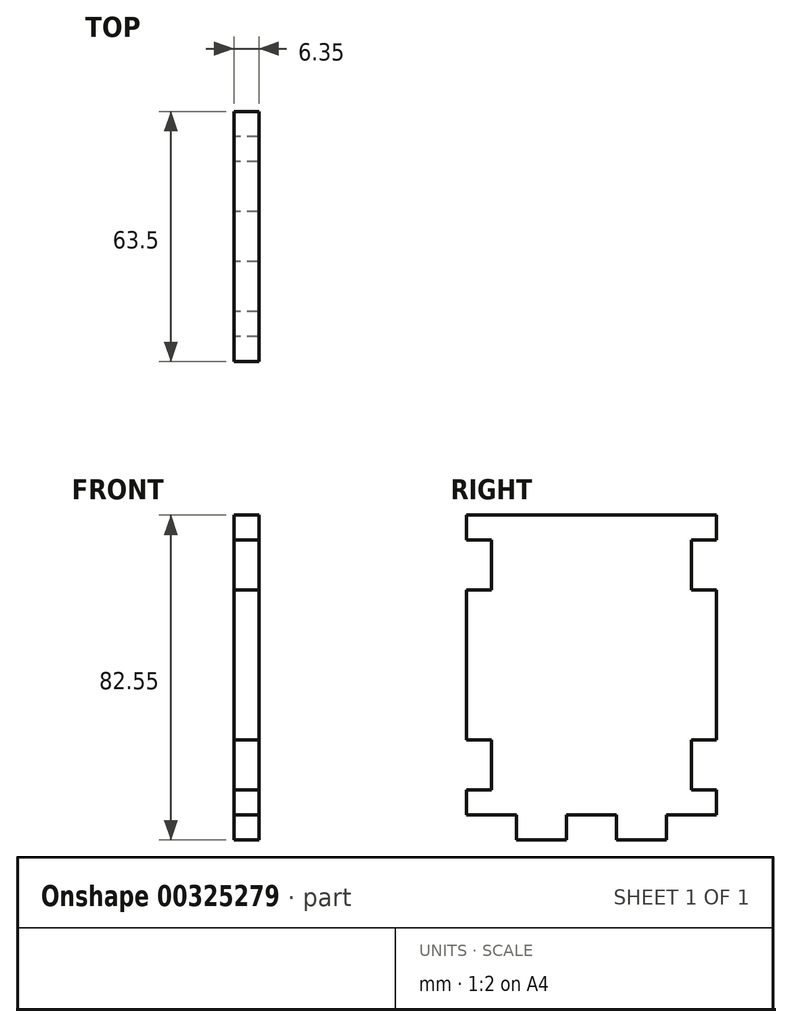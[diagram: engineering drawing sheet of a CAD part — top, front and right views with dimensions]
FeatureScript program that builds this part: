
annotation { "Feature Type Name" : "Feature", "Feature Type Description" : "" }
export const myFeature = defineFeature(function(context is Context, id is Id, definition is map)
    precondition{}
    {
        {
            var Q0;
            Q0=qCreatedBy(makeId("Right.planeOp"),FACE);
            var sketch = newSketch(context, id + "F0", { "sketchPlane" : qUnion([Q0])});
            skLineSegment(sketch, "E0", {"start": v(0, 6.35) * mm, "end": v(12.7, 6.35) * mm});
            skLineSegment(sketch, "E1", {"start": v(12.7, 6.35) * mm, "end": v(12.7, 0) * mm});
            skLineSegment(sketch, "E2", {"start": v(12.7, 0) * mm, "end": v(25.4, 0) * mm});
            skLineSegment(sketch, "E3", {"start": v(25.4, 0) * mm, "end": v(25.4, 6.35) * mm});
            skLineSegment(sketch, "E4", {"start": v(25.4, 6.35) * mm, "end": v(38.1, 6.35) * mm});
            skLineSegment(sketch, "E5", {"start": v(38.1, 6.35) * mm, "end": v(38.1, 0) * mm});
            skLineSegment(sketch, "E6", {"start": v(38.1, 0) * mm, "end": v(50.8, 0) * mm});
            skLineSegment(sketch, "E7", {"start": v(50.8, 0) * mm, "end": v(50.8, 6.35) * mm});
            skLineSegment(sketch, "E8", {"start": v(50.8, 6.35) * mm, "end": v(63.5, 6.35) * mm});
            skLineSegment(sketch, "E9", {"start": v(63.5, 6.35) * mm, "end": v(63.5, 12.7) * mm});
            skLineSegment(sketch, "E10", {"start": v(63.5, 12.7) * mm, "end": v(57.15, 12.7) * mm});
            skLineSegment(sketch, "E11", {"start": v(57.15, 12.7) * mm, "end": v(57.15, 25.4) * mm});
            skLineSegment(sketch, "E12", {"start": v(57.15, 25.4) * mm, "end": v(63.5, 25.4) * mm});
            skLineSegment(sketch, "E13", {"start": v(63.5, 25.4) * mm, "end": v(63.5, 63.5) * mm});
            skLineSegment(sketch, "E14", {"start": v(63.5, 63.5) * mm, "end": v(57.15, 63.5) * mm});
            skLineSegment(sketch, "E15", {"start": v(57.15, 63.5) * mm, "end": v(57.15, 76.2) * mm});
            skLineSegment(sketch, "E16", {"start": v(57.15, 76.2) * mm, "end": v(63.5, 76.2) * mm});
            skLineSegment(sketch, "E17", {"start": v(63.5, 76.2) * mm, "end": v(63.5, 82.55) * mm});
            skLineSegment(sketch, "E18", {"start": v(63.5, 82.55) * mm, "end": v(0, 82.55) * mm});
            skLineSegment(sketch, "E19", {"start": v(0, 82.55) * mm, "end": v(0, 76.2) * mm});
            skLineSegment(sketch, "E20", {"start": v(0, 76.2) * mm, "end": v(6.35, 76.2) * mm});
            skLineSegment(sketch, "E21", {"start": v(6.35, 76.2) * mm, "end": v(6.35, 63.5) * mm});
            skLineSegment(sketch, "E22", {"start": v(6.35, 63.5) * mm, "end": v(0, 63.5) * mm});
            skLineSegment(sketch, "E23", {"start": v(0, 63.5) * mm, "end": v(0, 25.4) * mm});
            skLineSegment(sketch, "E24", {"start": v(0, 25.4) * mm, "end": v(6.35, 25.4) * mm});
            skLineSegment(sketch, "E25", {"start": v(6.35, 25.4) * mm, "end": v(6.35, 12.7) * mm});
            skLineSegment(sketch, "E26", {"start": v(6.35, 12.7) * mm, "end": v(0, 12.7) * mm});
            skLineSegment(sketch, "E27", {"start": v(0, 12.7) * mm, "end": v(0, 6.35) * mm});
            skSolve(sketch);
        }
        {
            var Q0;
            Q0=makeQuery(id+"F0.imprint","IMPRINT",FACE,{"disambiguationData":[TD([[makeQuery(id+"F0.imprint","IMPRINT",EDGE,{"derivedFrom":sQuery(id+"F0.wireOp",EDGE,"E0")}),1.0]])]});
            extrude(context, id + "F1", {"entities" : qUnion([Q0]), "depth" : 6.35 * mm});
        }
    });
